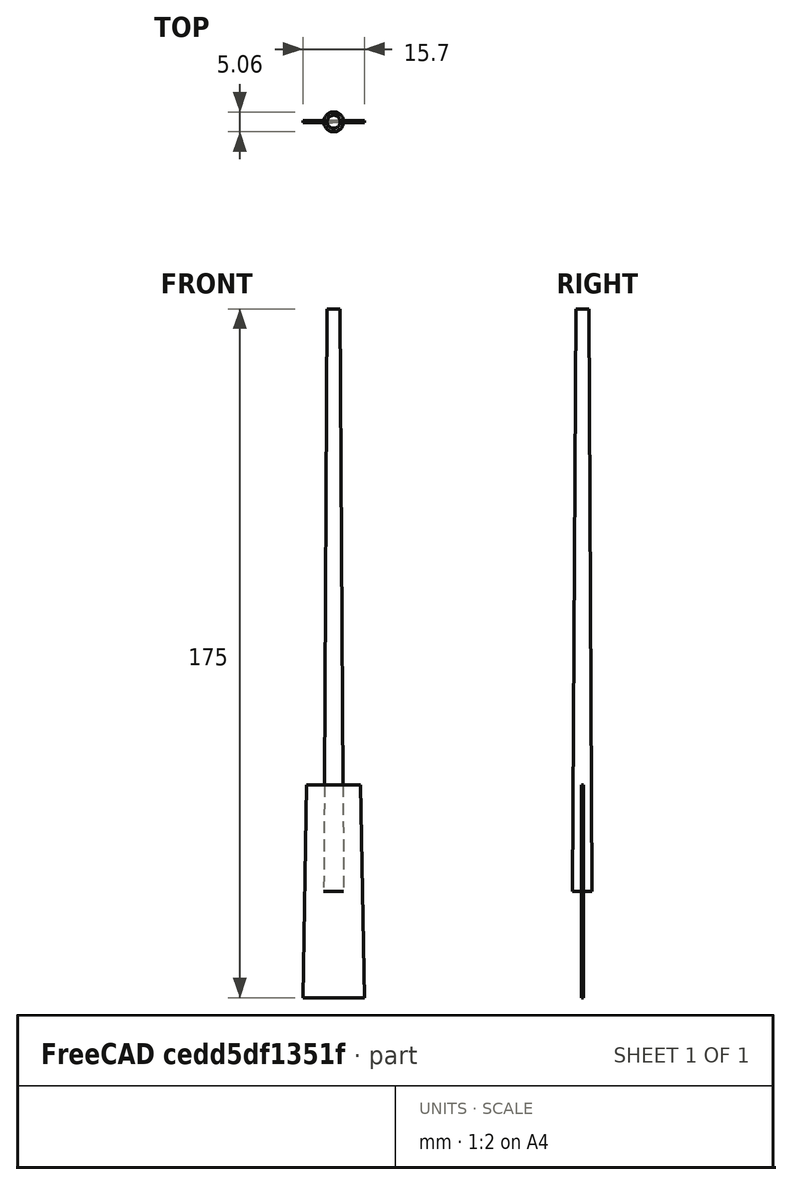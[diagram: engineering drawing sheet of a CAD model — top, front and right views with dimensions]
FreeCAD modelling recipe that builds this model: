
FCSTD DOCUMENT  (FreeCAD 0.21R33675 (Git))
Label: tapered_rolling_mandrel
License: Other
objects: TechDraw::DrawViewDimension×13, TechDraw::DrawProjGroupItem×6, TechDraw::DrawProjGroup×3, Sketcher::SketchObject×2, PartDesign::Body×2, Spreadsheet::Sheet×2, TechDraw::DrawSVGTemplate×2, TechDraw::DrawGeomHatch×2, TechDraw::DrawPage×2, PartDesign::Revolution×1, PartDesign::Pad×1, App::Part×1, App::DocumentObjectGroup×1, TechDraw::DrawViewAnnotation×1
note: 11 computed .brp shape members not serialized (recipe doc carries the construction recipe); baked Part::Feature solids carry a one-line shape summary decoded from their .brp

FEATURE [Sketcher::SketchObject] Sketch  label="s_mandrel_profile"
  FullyConstrained = true
  MapMode = 5
  Placement = pos=(0,0,0) rot=(1,0,0;1.5708rad)
  Support = -> [XZ_Plane]
  expr: Constraints[10] = Spreadsheet.mandrel_od_wide_end / 2
  expr: Constraints[13] = Spreadsheet.mandrel_length_protruding_either_side_staple
  expr: Constraints[14] = Spreadsheet.staple_length
  expr: Constraints[8] = Spreadsheet.mandrel_length
  expr: Constraints[9] = Spreadsheet.mandrel_od_narrow_end / 2
  sketch-geometry (6):
    g0: LineSegment StartX=0 StartY=148 StartZ=0 EndX=1.65338 EndY=148 EndZ=0
    g1: LineSegment StartX=1.65338 StartY=148 StartZ=0 EndX=2.52578 EndY=0 EndZ=0
    g2: LineSegment StartX=2.52578 StartY=0 StartZ=0 EndX=0 EndY=0 EndZ=0
    g3: LineSegment StartX=0 StartY=0 StartZ=0 EndX=0 EndY=148 EndZ=0
    g4: GeomPoint X=2.24873 Y=47 Z=0
    g5: GeomPoint X=1.93042 Y=101 Z=0
  constraints (15):
    c: PointOnObject(g0,g-2)
    c: Horizontal(g0)
    c: Coincident(g0,g1)
    c: PointOnObject(g1,g-1)
    c: Coincident(g1,g2)
    c: Coincident(g2,g-1)
    c: Coincident(g2,g3)
    c: Coincident(g3,g0)
    c: DistanceY(g3,g3) = 148
    c: DistanceX(g0,g0) = 1.65338
    c: DistanceX(g2,g2) = 2.52578
    c: PointOnObject(g4,g1)
    c: PointOnObject(g5,g1)
    c: DistanceY(g1,g4) = 47
    c: DistanceY(g4,g5) = 54
FEATURE [PartDesign::Revolution] Revolution  label="rev_mandrel"
  Angle = 360
  Axis = (0,-2e-16,1)
  Base = (0,0,0)
  Placement = pos=(0,0,0) rot=(1,0,0;1.5708rad)
  Profile = -> Sketch
  ReferenceAxis = -> Sketch [V_Axis]
FEATURE [PartDesign::Body] Body  label="b_mandrel"
  Group = -> [Sketch,Revolution]
  Origin = -> Origin
  Tip = -> Revolution
FEATURE [Spreadsheet::Sheet] Spreadsheet  label="spr_dimensions"
  cells = A1='Input parameters (all dimensions in mm); if you know the sheet metal staple blank end widths, input those here; otherwise, input the inner diameters (IDs) of the staple at each end, in column E (see column D header FMI); D1='Calculated quantities (all lengths in mm; angles in degrees); if you only know the staple IDs, and not the blank dimensions, you can put those directory in here, overwriting the equations; the staple blank end widths will be calculated for you to the right; G1='Staple blank end widths calculated from staple IDs (mm); A2='staple_length; B2(staple_length)==54 mm; D2='staple_id_narrow_end; E2(staple_id_narrow_end)==staple_blank_width_narrow_end / pi - staple_blank_material_thickness; G2='staple_blank_width_wide_end_from_ID_final; H2(staple_blank_width_wide_end_from_ID_final)==pi * (staple_id_wide_end + staple_blank_material_thickness); A3='staple_blank_width_wide_end; B3(staple_blank_width_wide_end)==15.7 mm; D3='staple_id_wide_end; E3(staple_id_wide_end)==staple_blank_width_wide_end / pi - staple_blank_material_thickness; G3='staple_blank_width_narrow_end_from_ID_final; H3(staple_blank_width_narrow_end_from_ID_final)==pi * (staple_id_narrow_end + staple_blank_material_thickness); A4='staple_blank_width_narrow_end; B4(staple_blank_width_narrow_end)==13.7 mm; D4='mandrel_od_wide_end; E4(mandrel_od_wide_end)==staple_id_wide_end + (mandrel_length - staple_length) * tan(mandrel_taper_angle); A5='staple_blank_material_thickness; B5(staple_blank_material_thickness)==0.5 mm; D5='mandrel_od_narrow_end; E5(mandrel_od_narrow_end)==staple_id_narrow_end - (mandrel_length - staple_length) * tan(mandrel_taper_angle); D6='mandrel_taper_angle; E6(mandrel_taper_angle)==atan((staple_id_wide_end - staple_id_narrow_end) / (2 * staple_length)); A7='mandrel_length; B7(mandrel_length)==148 mm; D7='mandrel_length_protruding_either_side_staple; E7(mandrel_length_protruding_either_side_staple)==(mandrel_length - staple_length) / 2
FEATURE [TechDraw::DrawSVGTemplate] Template001
  EditableTexts = Designed_by_Name=Designed by Name; Drawing_number=Drawing number; FC-Date=Date; FC-SC=Scale; FC-SH=Sheet; FC-Title=Staple Blank and Mandrel; Subtitle=All dimensions in mm and degrees; Weight=Weight
  Height = 210
  Orientation = 1
  Width = 297
FEATURE [TechDraw::DrawProjGroupItem] ProjItem  label="Front"
  Caption = Mandrel
  CoarseView = false
  Direction = (0,-1,0)
  Focus = 100
  HardHidden = false
  IsoCount = 0
  IsoHidden = false
  IsoVisible = false
  LockPosition = true
  Perspective = false
  Rotation = 0
  RotationVector = (1,0,0)
  ScaleType = 2
  ScrubCount = 0
  SeamHidden = false
  SeamVisible = true
  SmoothHidden = false
  SmoothVisible = true
  Source = -> [Body]
  Type = 0
  X = 0
  XDirection = (1e-16,0,-1)
  Y = 0
FEATURE [TechDraw::DrawProjGroup] ProjGroup  label="pg_mandrel"
  Anchor = -> ProjItem
  AutoDistribute = true
  LockPosition = false
  ProjectionType = 0
  Rotation = 0
  ScaleType = 0
  Source = -> [Body]
  Views = -> [ProjItem]
  X = 150.932
  Y = 91.3289
  spacingX = 15
  spacingY = 15
FEATURE [TechDraw::DrawViewDimension] Dimension
  AngleOverride = false
  Arbitrary = false
  ArbitraryTolerances = false
  EqualTolerance = true
  ExtensionAngle = 0
  FormatSpec = %.2f
  FormatSpecOverTolerance = %+.2f
  FormatSpecUnderTolerance = %+.2f
  Inverted = false
  LineAngle = 0
  LockPosition = false
  MeasureType = 1
  OverTolerance = 0
  References2D = -> [ProjItem]
  Rotation = 0
  ScaleType = 0
  TheoreticalExact = false
  Type = 2
  UnderTolerance = 0
  X = 73.5933
  Y = 26.0669
FEATURE [TechDraw::DrawViewDimension] Dimension001
  AngleOverride = false
  Arbitrary = false
  ArbitraryTolerances = false
  EqualTolerance = true
  ExtensionAngle = 0
  FormatSpec = %.2f
  FormatSpecOverTolerance = %+.2f
  FormatSpecUnderTolerance = %+.2f
  Inverted = false
  LineAngle = 0
  LockPosition = false
  MeasureType = 1
  OverTolerance = 0
  References2D = -> [ProjItem]
  Rotation = 0
  ScaleType = 0
  TheoreticalExact = false
  Type = 2
  UnderTolerance = 0
  X = -78.166
  Y = 20.5315
FEATURE [TechDraw::DrawViewDimension] Dimension002
  AngleOverride = false
  Arbitrary = false
  ArbitraryTolerances = false
  EqualTolerance = true
  ExtensionAngle = 0
  FormatSpec = %.2f
  FormatSpecOverTolerance = %+.2f
  FormatSpecUnderTolerance = %+.2f
  Inverted = false
  LineAngle = 0
  LockPosition = false
  MeasureType = 1
  OverTolerance = 0
  References2D = -> [ProjItem]
  Rotation = 0
  ScaleType = 0
  TheoreticalExact = false
  Type = 1
  UnderTolerance = 0
  X = -0.974764
  Y = -21.9551
FEATURE [Sketcher::SketchObject] Sketch001  label="s_staple_blank"
  FullyConstrained = true
  MapMode = 5
  Placement = pos=(0,0,0) rot=(1,0,0;1.5708rad)
  Support = -> [XZ_Plane002]
  expr: Constraints[6] = Spreadsheet.staple_length / 2
  expr: Constraints[7] = Spreadsheet.staple_length / 2
  expr: Constraints[8] = Spreadsheet.staple_blank_width_wide_end_from_ID_final
  expr: Constraints[9] = Spreadsheet.staple_blank_width_narrow_end_from_ID_final
  sketch-geometry (4):
    g0: LineSegment StartX=-7.85 StartY=-27 StartZ=0 EndX=7.85 EndY=-27 EndZ=0
    g1: LineSegment StartX=7.85 StartY=-27 StartZ=0 EndX=6.85 EndY=27 EndZ=0
    g2: LineSegment StartX=6.85 StartY=27 StartZ=0 EndX=-6.85 EndY=27 EndZ=0
    g3: LineSegment StartX=-6.85 StartY=27 StartZ=0 EndX=-7.85 EndY=-27 EndZ=0
  constraints (10):
    c: Coincident(g0,g1)
    c: Coincident(g1,g2)
    c: Coincident(g2,g3)
    c: Coincident(g3,g0)
    c: Symmetric(g0,g0,g-2)
    c: Symmetric(g1,g2,g-2)
    c: DistanceY(g-1,g1) = 27
    c: DistanceY(g0,g-1) = 27
    c: DistanceX(g0,g0) = 15.7
    c: DistanceX(g2,g2) = 13.7
FEATURE [PartDesign::Pad] Pad  label="p_staple_blank"
  Direction = (0,-1,-2e-16)
  Length = 0.5
  Length2 = 10
  Midplane = true
  Placement = pos=(0,0,0) rot=(1,0,0;1.5708rad)
  Profile = -> Sketch001
  ReferenceAxis = -> Sketch001 [N_Axis]
  Type = 0
  expr: Length = Spreadsheet.staple_blank_material_thickness
FEATURE [PartDesign::Body] Body001  label="b_staple_blank"
  Group = -> [Sketch001,Pad]
  Origin = -> Origin002
  Tip = -> Pad
FEATURE [TechDraw::DrawProjGroupItem] ProjItem001  label="Front001"
  Caption = Staple Blank Front
  CoarseView = false
  Direction = (0,-1,0)
  Focus = 100
  HardHidden = false
  IsoCount = 0
  IsoHidden = false
  IsoVisible = false
  LockPosition = true
  Perspective = false
  Rotation = 0
  RotationVector = (1,0,0)
  ScaleType = 2
  ScrubCount = 0
  SeamHidden = false
  SeamVisible = true
  SmoothHidden = false
  SmoothVisible = true
  Source = -> [Body001]
  Type = 0
  X = 0
  XDirection = (1,0,0)
  Y = 0
FEATURE [TechDraw::DrawProjGroupItem] ProjItem002  label="Left"
  Caption = Side
  CoarseView = false
  Direction = (-1,-1e-16,0)
  Focus = 100
  HardHidden = false
  IsoCount = 0
  IsoHidden = false
  IsoVisible = false
  LockPosition = false
  Perspective = false
  Rotation = 0
  RotationVector = (1,0,0)
  ScaleType = 2
  ScrubCount = 0
  SeamHidden = false
  SeamVisible = true
  SmoothHidden = false
  SmoothVisible = true
  Source = -> [Body001]
  Type = 1
  X = 30.75
  XDirection = (1e-16,-1,0)
  Y = 0
FEATURE [TechDraw::DrawProjGroup] ProjGroup001  label="pg_staple_blank"
  Anchor = -> ProjItem001
  AutoDistribute = false
  LockPosition = false
  ProjectionType = 0
  Rotation = 0
  ScaleType = 0
  Source = -> [Body001]
  Views = -> [ProjItem001,ProjItem002]
  X = 133.07
  Y = 148.205
  spacingX = 25
  spacingY = 25
FEATURE [TechDraw::DrawViewDimension] Dimension004
  AngleOverride = false
  Arbitrary = false
  ArbitraryTolerances = false
  EqualTolerance = true
  ExtensionAngle = 0
  FormatSpec = %.2f
  FormatSpecOverTolerance = %+.2f
  FormatSpecUnderTolerance = %+.2f
  Inverted = false
  LineAngle = 0
  LockPosition = false
  MeasureType = 1
  OverTolerance = 0
  References2D = -> [ProjItem002]
  Rotation = 0
  ScaleType = 0
  TheoreticalExact = false
  Type = 1
  UnderTolerance = 0
  X = 29.823
  Y = 25.4043
FEATURE [TechDraw::DrawViewDimension] Dimension005
  AngleOverride = false
  Arbitrary = false
  ArbitraryTolerances = false
  EqualTolerance = true
  ExtensionAngle = 0
  FormatSpec = %.2f
  FormatSpecOverTolerance = %+.2f
  FormatSpecUnderTolerance = %+.2f
  Inverted = false
  LineAngle = 0
  LockPosition = false
  MeasureType = 1
  OverTolerance = 0
  References2D = -> [ProjItem001]
  Rotation = 0
  ScaleType = 0
  TheoreticalExact = false
  Type = 2
  UnderTolerance = 0
  X = -30.4214
  Y = 0.246347
FEATURE [TechDraw::DrawViewDimension] Dimension006
  AngleOverride = false
  Arbitrary = false
  ArbitraryTolerances = false
  EqualTolerance = true
  ExtensionAngle = 0
  FormatSpec = %.2f
  FormatSpecOverTolerance = %+.2f
  FormatSpecUnderTolerance = %+.2f
  Inverted = false
  LineAngle = 0
  LockPosition = false
  MeasureType = 1
  OverTolerance = 0
  References2D = -> [ProjItem001]
  Rotation = 0
  ScaleType = 0
  TheoreticalExact = false
  Type = 1
  UnderTolerance = 0
  X = -0.760037
  Y = 44.6284
FEATURE [TechDraw::DrawViewDimension] Dimension007
  AngleOverride = false
  Arbitrary = false
  ArbitraryTolerances = false
  EqualTolerance = true
  ExtensionAngle = 0
  FormatSpec = %.2f
  FormatSpecOverTolerance = %+.2f
  FormatSpecUnderTolerance = %+.2f
  Inverted = false
  LineAngle = 0
  LockPosition = false
  MeasureType = 1
  OverTolerance = 0
  References2D = -> [ProjItem001]
  Rotation = 0
  ScaleType = 0
  TheoreticalExact = false
  Type = 1
  UnderTolerance = 0
  X = -26.2739
  Y = -29.7984
FEATURE [TechDraw::DrawViewDimension] Dimension008
  AngleOverride = false
  Arbitrary = false
  ArbitraryTolerances = false
  EqualTolerance = true
  ExtensionAngle = 0
  FormatSpec = %.2f
  FormatSpecOverTolerance = %+.2f
  FormatSpecUnderTolerance = %+.2f
  Inverted = false
  LineAngle = 0
  LockPosition = false
  MeasureType = 1
  OverTolerance = 0
  References2D = -> [ProjItem001]
  Rotation = 0
  ScaleType = 0
  TheoreticalExact = false
  Type = 1
  UnderTolerance = 0
  X = -17.3837
  Y = 34.8258
FEATURE [TechDraw::DrawGeomHatch] GeomHatch  label="GeomHatchFX0"
  FilePattern = <path>
  NamePattern = Diamond
  PatternOffset = (0,0,0)
  PatternRotation = 0
  ScalePattern = 1
  Source = -> ProjItem001 [Face0]
FEATURE [TechDraw::DrawViewDimension] Dimension009
  AngleOverride = false
  Arbitrary = false
  ArbitraryTolerances = false
  EqualTolerance = true
  ExtensionAngle = 0
  FormatSpec = %.2f
  FormatSpecOverTolerance = %+.2f
  FormatSpecUnderTolerance = %+.2f
  Inverted = false
  LineAngle = 0
  LockPosition = false
  MeasureType = 1
  OverTolerance = 0
  References2D = -> [ProjItem001]
  Rotation = 0
  ScaleType = 0
  TheoreticalExact = false
  Type = 6
  UnderTolerance = 0
  X = 17.0454
  Y = 37.439
FEATURE [TechDraw::DrawGeomHatch] GeomHatch001  label="GeomHatch001FX0"
  FilePattern = <path>
  NamePattern = Diamond
  PatternOffset = (0,0,0)
  PatternRotation = 0
  ScalePattern = 1
  Source = -> ProjItem [Face0]
FEATURE [TechDraw::DrawViewDimension] Dimension010
  AngleOverride = false
  Arbitrary = false
  ArbitraryTolerances = false
  EqualTolerance = true
  ExtensionAngle = 0
  FormatSpec = %.2f
  FormatSpecOverTolerance = %+.2f
  FormatSpecUnderTolerance = %+.2f
  Inverted = false
  LineAngle = 0
  LockPosition = false
  MeasureType = 1
  OverTolerance = 0
  References2D = -> [ProjItem]
  Rotation = 0
  ScaleType = 0
  TheoreticalExact = false
  Type = 6
  UnderTolerance = 0
  X = -122.949
  Y = 15.0352
FEATURE [TechDraw::DrawPage] Page001  label="td_mandrel"
  KeepUpdated = true
  NextBalloonIndex = 1
  ProjectionType = 0
  Template = -> Template001
  Views = -> [ProjGroup,Dimension,Dimension001,Dimension002,ProjGroup001,Dimension004,Dimension005,Dimension006,Dimension007,Dimension008,Dimension009,Dimension010]
FEATURE [App::Part] Part  label="p_mandrel_staple_blank"
  Group = -> [Body,Spreadsheet,Body001,Page001]
  Origin = -> Origin001
FEATURE [Spreadsheet::Sheet] Spreadsheet001  label="LICENSE"
  cells = A1='Licensed under the TAPR Open Hardware License (www.tapr.org/OHL)
FEATURE [App::DocumentObjectGroup] Group  label="technical_drawings_CNC"
FEATURE [TechDraw::DrawSVGTemplate] Template002
  EditableTexts = Designed_by_Name=Designed by Name; Drawing_number=Drawing number; FC-Date=Date; FC-SC=Scale; FC-SH=Sheet; FC-Title=tolerances; Subtitle=all units in mm; Weight=Weight
  Height = 210
  Orientation = 1
  Template = <path>
  Width = 297
FEATURE [TechDraw::DrawProjGroupItem] ProjItem003  label="Front002"
  CoarseView = false
  Direction = (-1,-4e-16,-1e-16)
  Focus = 100
  HardHidden = false
  IsoCount = 0
  IsoHidden = false
  IsoVisible = false
  LockPosition = true
  Perspective = false
  Rotation = 0
  RotationVector = (1,0,0)
  ScaleType = 2
  ScrubCount = 0
  SeamHidden = false
  SeamVisible = true
  SmoothHidden = false
  SmoothVisible = true
  Source = -> [Body]
  Type = 0
  X = 0
  XDirection = (-1e-16,5e-16,1)
  Y = 0
FEATURE [TechDraw::DrawProjGroupItem] ProjItem004  label="Right"
  CoarseView = false
  Direction = (-2e-16,5e-16,1)
  Focus = 100
  HardHidden = false
  IsoCount = 0
  IsoHidden = false
  IsoVisible = false
  LockPosition = false
  Perspective = false
  Rotation = 0
  RotationVector = (1,0,0)
  ScaleType = 2
  ScrubCount = 0
  SeamHidden = false
  SeamVisible = true
  SmoothHidden = false
  SmoothVisible = true
  Source = -> [Body]
  Type = 2
  X = 105.573
  XDirection = (1,4e-16,2e-16)
  Y = 0
FEATURE [TechDraw::DrawProjGroupItem] ProjItem005  label="Left001"
  CoarseView = false
  Direction = (0,-5e-16,-1)
  Focus = 100
  HardHidden = false
  IsoCount = 0
  IsoHidden = false
  IsoVisible = false
  LockPosition = false
  Perspective = false
  Rotation = 0
  RotationVector = (1,0,0)
  ScaleType = 2
  ScrubCount = 0
  SeamHidden = false
  SeamVisible = true
  SmoothHidden = false
  SmoothVisible = true
  Source = -> [Body]
  Type = 1
  X = -103.626
  XDirection = (-1,-4e-16,0)
  Y = 0
FEATURE [TechDraw::DrawProjGroup] ProjGroup002
  Anchor = -> ProjItem003
  AutoDistribute = false
  LockPosition = false
  ProjectionType = 0
  Rotation = 0
  ScaleType = 0
  Source = -> [Body]
  Views = -> [ProjItem003,ProjItem004,ProjItem005]
  X = 148.5
  Y = 105
  spacingX = 15
  spacingY = 15
FEATURE [TechDraw::DrawViewDimension] Dimension011
  AngleOverride = false
  Arbitrary = false
  ArbitraryTolerances = false
  EqualTolerance = true
  ExtensionAngle = 0
  FormatSpec = ⌀%.2f
  FormatSpecOverTolerance = %+.2f
  FormatSpecUnderTolerance = %+.2f
  Inverted = false
  LineAngle = 0
  LockPosition = false
  MeasureType = 1
  OverTolerance = 0.01
  References2D = -> [ProjItem005]
  Rotation = 0
  ScaleType = 0
  TheoreticalExact = false
  Type = 5
  UnderTolerance = -0.01
  X = -11.3407
  Y = 28.8492
FEATURE [TechDraw::DrawViewDimension] Dimension012
  AngleOverride = false
  Arbitrary = false
  ArbitraryTolerances = false
  EqualTolerance = true
  ExtensionAngle = 0
  FormatSpec = ⌀%.2f
  FormatSpecOverTolerance = %+.2f
  FormatSpecUnderTolerance = %+.2f
  Inverted = false
  LineAngle = 0
  LockPosition = false
  MeasureType = 1
  OverTolerance = 0.01
  References2D = -> [ProjItem004]
  Rotation = 0
  ScaleType = 0
  TheoreticalExact = false
  Type = 5
  UnderTolerance = -0.01
  X = 8.55528
  Y = 26.4617
FEATURE [TechDraw::DrawViewDimension] Dimension013
  AngleOverride = false
  Arbitrary = false
  ArbitraryTolerances = false
  EqualTolerance = true
  ExtensionAngle = 0
  FormatSpec = %.2f
  FormatSpecOverTolerance = %+.2f
  FormatSpecUnderTolerance = %+.2f
  Inverted = false
  LineAngle = 0
  LockPosition = false
  MeasureType = 1
  OverTolerance = 0
  References2D = -> [ProjItem003]
  Rotation = 0
  ScaleType = 0
  TheoreticalExact = false
  Type = 1
  UnderTolerance = 0
  X = -0.4974
  Y = 35.3136
FEATURE [TechDraw::DrawViewAnnotation] Annotation
  Font = Fira Sans Book
  LineSpace = 100
  LockPosition = false
  MaxWidth = -1
  Rotation = 0
  ScaleType = 0
  Text = rolling_mandrel_D_concert_pitch_Rowesome
  TextSize = 5
  TextStyle = 0
  X = 152.648
  Y = 74.7426
FEATURE [TechDraw::DrawPage] Page002  label="mandrel_CNC_tolerances"
  KeepUpdated = true
  NextBalloonIndex = 1
  ProjectionType = 0
  Template = -> Template002
  Views = -> [ProjGroup002,Dimension011,Dimension012,Dimension013,Annotation]
note: 3 file-system paths scrubbed to <path> (originals preserved in the JSON sidecar)
